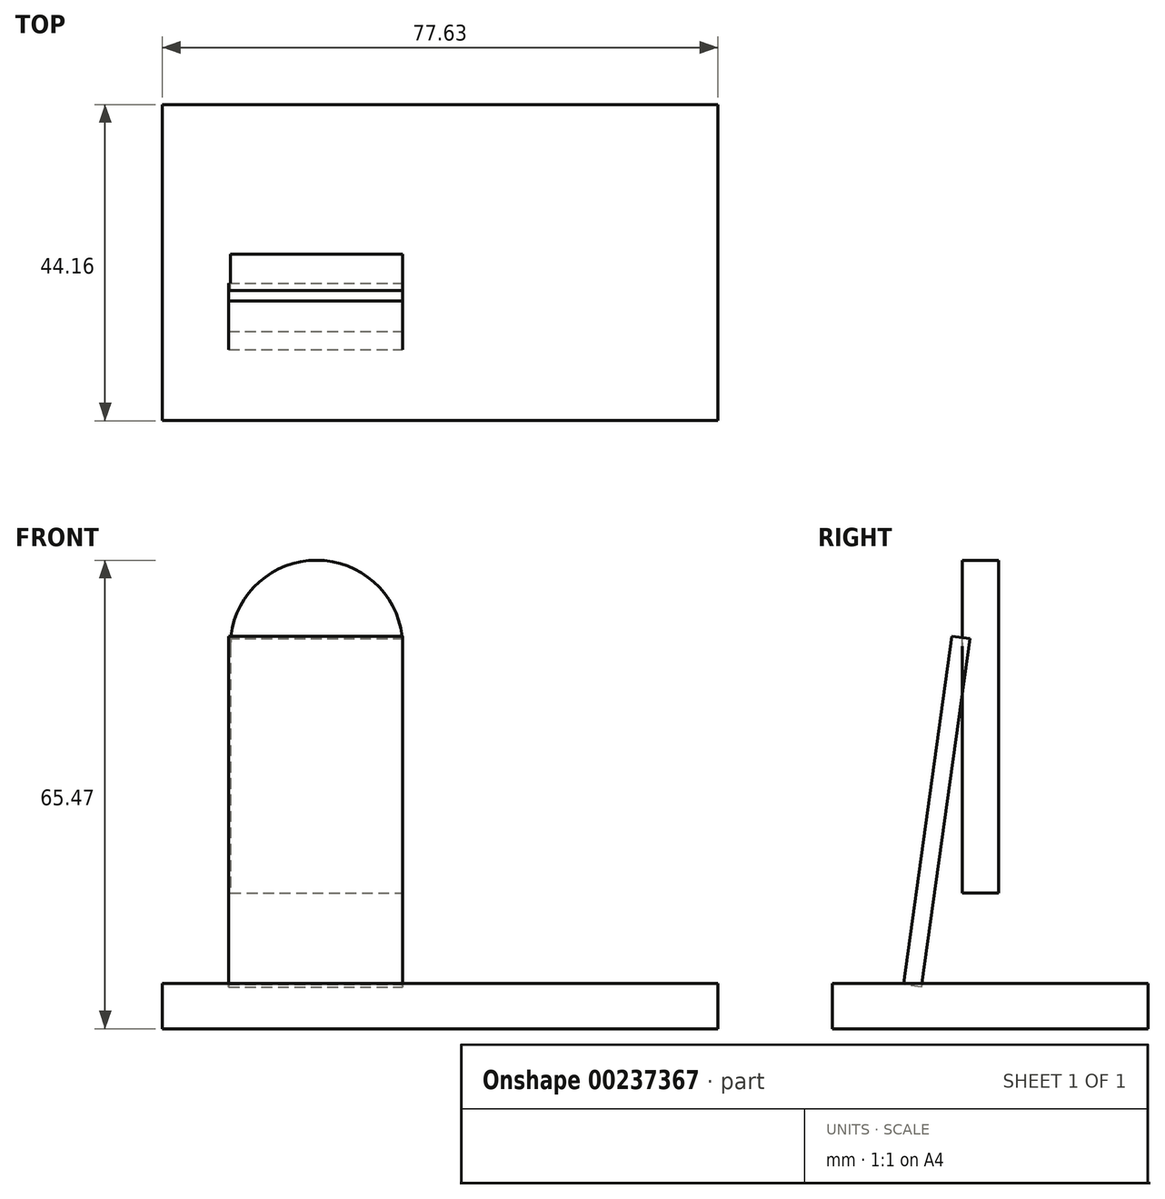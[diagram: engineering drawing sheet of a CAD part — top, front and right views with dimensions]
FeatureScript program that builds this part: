
annotation { "Feature Type Name" : "Feature", "Feature Type Description" : "" }
export const myFeature = defineFeature(function(context is Context, id is Id, definition is map)
    precondition{}
    {
        {
            var Q0;
            Q0=qCreatedBy(makeId("Top.planeOp"),FACE);
            var sketch = newSketch(context, id + "F0", { "sketchPlane" : qUnion([Q0])});
            skLineSegment(sketch, "E0.bottom", {"start": v(-33.6, 20.9) * mm, "end": v(44.04, 20.9) * mm});
            skLineSegment(sketch, "E0.top", {"start": v(-33.6, -23.27) * mm, "end": v(44.04, -23.27) * mm});
            skLineSegment(sketch, "E0.left", {"start": v(-33.6, 20.9) * mm, "end": v(-33.6, -23.27) * mm});
            skLineSegment(sketch, "E0.right", {"start": v(44.04, 20.9) * mm, "end": v(44.04, -23.27) * mm});
            skPoint(sketch, "E1", {"position": v(-26, -14) * mm});
            skPoint(sketch, "E2", {"position": v(-6.77, -14) * mm});
            skSolve(sketch);
        }
        {
            var Q0;
            Q0=makeQuery(id+"F0.imprint","IMPRINT",FACE,{"disambiguationData":[TD([[makeQuery(id+"F0.imprint","IMPRINT",EDGE,{"derivedFrom":sQuery(id+"F0.wireOp",EDGE,"E0.bottom")}),-1.0]])]});
            extrude(context, id + "F1", {"entities" : qUnion([Q0]), "depth" : 6.35 * mm});
        }
        {
            var Q0;
            Q0=qCreatedBy(makeId("Front.planeOp"),FACE);
            var sketch = newSketch(context, id + "F2", { "sketchPlane" : qUnion([Q0])});
            skLineSegment(sketch, "E3.bottom", {"start": v(-24.1, 53.42) * mm, "end": v(0, 53.42) * mm});
            skLineSegment(sketch, "E3.top", {"start": v(-24.1, 19) * mm, "end": v(0, 19) * mm});
            skLineSegment(sketch, "E3.left", {"start": v(-24.1, 53.42) * mm, "end": v(-24.1, 19) * mm});
            skLineSegment(sketch, "E3.right", {"start": v(0, 53.42) * mm, "end": v(0, 19) * mm});
            skArc(sketch, "E4", {"start": v(0, 53.42) * mm, "mid": v(-12.05, 65.47) * mm, "end": v(-24.1, 53.42) * mm});
            skSolve(sketch);
        }
        {
            var Q0;
            Q0=makeQuery(id+"F2.imprint","IMPRINT",FACE,{"disambiguationData":[TD([[makeQuery(id+"F2.imprint","IMPRINT",EDGE,{"derivedFrom":sQuery(id+"F2.wireOp",EDGE,"E3.bottom")}),1.0]])]});
            var Q1;
            Q1=makeQuery(id+"F2.imprint","IMPRINT",FACE,{"disambiguationData":[TD([[makeQuery(id+"F2.imprint","IMPRINT",EDGE,{"derivedFrom":sQuery(id+"F2.wireOp",EDGE,"E3.bottom")}),-1.0]])]});
            extrude(context, id + "F3", {"entities" : qUnion([Q0, Q1]), "depth" : 5.08 * mm});
        }
        {
            var Q0;
            Q0=makeQuery(id+"F1.opExtrude","CAP_FACE",FACE,{"disambiguationData":[OSD([sQuery(id+"F0.wireOp",EDGE,"E0.bottom"),sQuery(id+"F0.wireOp",EDGE,"E0.top"),sQuery(id+"F0.wireOp",EDGE,"E0.left"),sQuery(id+"F0.wireOp",EDGE,"E0.right")])],"isStart":false});
            cPlane(context, id + "F4", {"entities" : qUnion([Q0]), "cplaneType" : CPlaneType.OFFSET, "offset" : 0 * mm, "width" : 152.4 * mm, "height" : 152.4 * mm});
        }
        {
            var Q0;
            Q0=qCreatedBy(id+"F4.planeOp",FACE);
            var sketch = newSketch(context, id + "F5", { "sketchPlane" : qUnion([Q0])});
            skPoint(sketch, "E5", {"position": v(-24.1, -13.3) * mm});
            skPoint(sketch, "E6", {"position": v(0, -13.3) * mm});
            skSolve(sketch);
        }
        {
            var Q0;
            Q0=qCreatedBy(id+"F4.planeOp",FACE);
            var sketch = newSketch(context, id + "F6", { "sketchPlane" : qUnion([Q0])});
            skLineSegment(sketch, "E7.0", {"start": v(-24.1, -5.08) * mm, "end": v(0, -5.08) * mm});
            skLineSegment(sketch, "E8.top", {"start": v(-24.1, -13.13) * mm, "end": v(0, -13.13) * mm});
            skLineSegment(sketch, "E8.left", {"start": v(-24.1, -5.08) * mm, "end": v(-24.1, -13.13) * mm});
            skLineSegment(sketch, "E8.right", {"start": v(0, -5.08) * mm, "end": v(0, -13.13) * mm});
            skSolve(sketch);
        }
        {
            var Q0;
            Q0=sQuery(id+"F6.wireOp",EDGE,"E8.top");
            cPoint(context, id + "F7", {"entities" : qUnion([Q0]), "parameter" : 0.5});
        }
        {
            var Q0;
            Q0=sQuery(id+"F6.wireOp",EDGE,"E7.0");
            cPoint(context, id + "F8", {"entities" : qUnion([Q0]), "parameter" : 0.5});
        }
        {
            var Q0;
            Q0=makeQuery(id+"F3.opExtrude","CAP_EDGE",EDGE,{"disambiguationData":[OSD([sQuery(id+"F2.wireOp",EDGE,"E4")])],"isStart":false});
            cPoint(context, id + "F9", {"entities" : qUnion([Q0]), "parameter" : 0.5});
        }
        {
            var Q0;
            Q0 = qCreatedBy(id + "F7" ,VERTEX);
            var Q1;
            Q1 = qCreatedBy(id + "F8" ,VERTEX);
            var Q2;
            Q2 = qCreatedBy(id + "F9" ,VERTEX);
            cPlane(context, id + "F10", {"entities" : qUnion([Q0, Q1, Q2]), "cplaneType" : CPlaneType.THREE_POINT, "offset" : 25.4 * mm, "width" : 152.4 * mm, "height" : 152.4 * mm});
        }
        {
            var Q0;
            Q0=makeQuery(id+"F3.opExtrude","CAP_EDGE",EDGE,{"disambiguationData":[OSD([sQuery(id+"F2.wireOp",EDGE,"E4")])],"isStart":false});
            cPoint(context, id + "F11", {"entities" : qUnion([Q0]), "parameter" : 0.5});
        }
        {
            var Q0;
            Q0=sQuery(id+"F5.wireOp",VERTEX,"E5");
            var Q1;
            Q1=sQuery(id+"F5.wireOp",VERTEX,"E6");
            var Q2;
            Q2 = qCreatedBy(id + "F11" ,VERTEX);
            cPlane(context, id + "F12", {"entities" : qUnion([Q0, Q1, Q2]), "cplaneType" : CPlaneType.THREE_POINT, "offset" : 25.4 * mm, "width" : 152.4 * mm, "height" : 152.4 * mm});
        }
        {
            var Q0;
            Q0=qCreatedBy(id+"F12.planeOp",FACE);
            var sketch = newSketch(context, id + "F13", { "sketchPlane" : qUnion([Q0])});
            skLineSegment(sketch, "E9.bottom", {"start": v(24.34, 53.42) * mm, "end": v(0, 53.42) * mm});
            skLineSegment(sketch, "E9.top", {"start": v(24.34, 4.28) * mm, "end": v(0, 4.28) * mm});
            skLineSegment(sketch, "E9.left", {"start": v(24.34, 53.42) * mm, "end": v(24.34, 4.28) * mm});
            skLineSegment(sketch, "E9.right", {"start": v(0, 53.42) * mm, "end": v(0, 4.28) * mm});
            skSolve(sketch);
        }
        {
            var Q0;
            Q0 = qSketchRegion(id + "F13", true);
            extrude(context, id + "F14", {"entities" : qUnion([Q0]), "depth" : 2.54 * mm});
        }
    });
